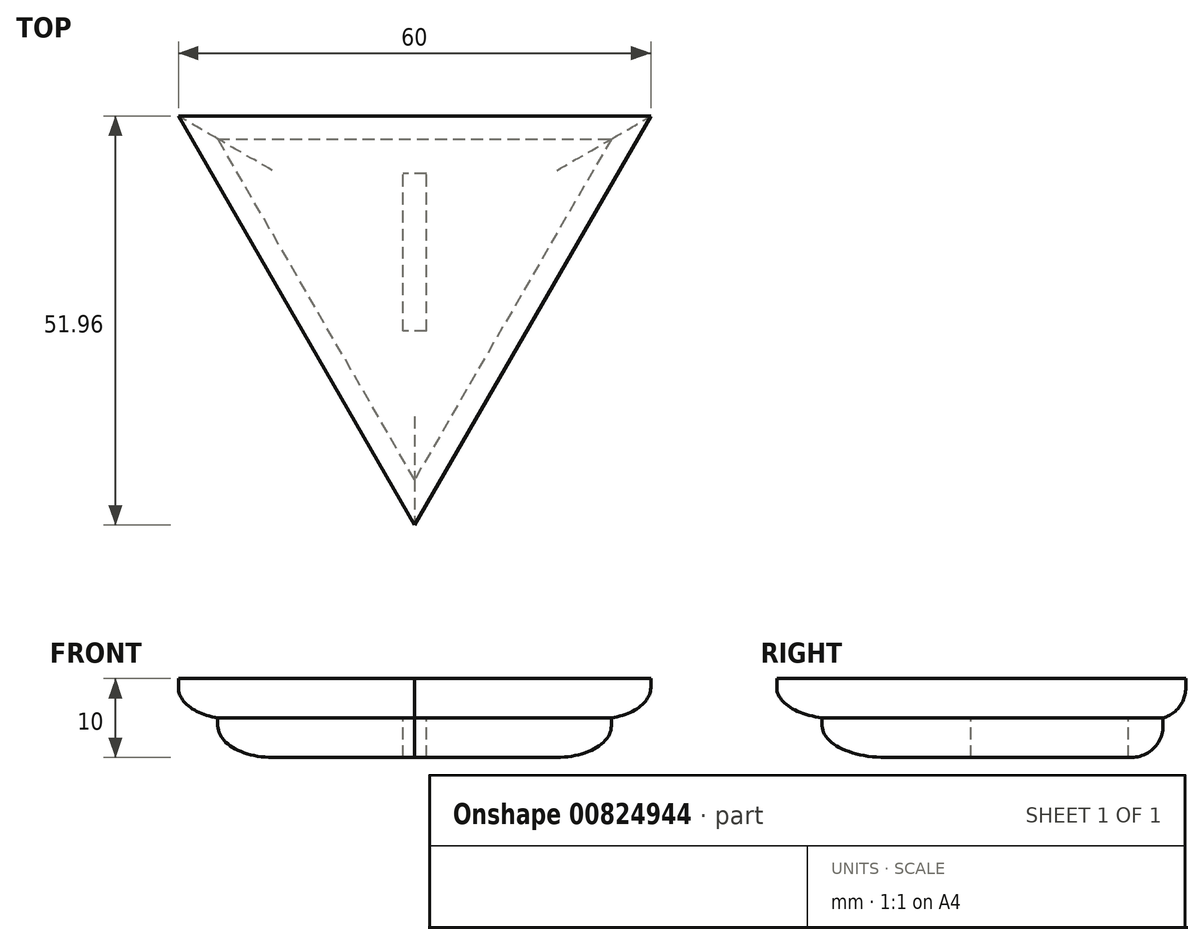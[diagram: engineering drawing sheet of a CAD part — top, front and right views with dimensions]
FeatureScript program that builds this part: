
annotation { "Feature Type Name" : "Feature", "Feature Type Description" : "" }
export const myFeature = defineFeature(function(context is Context, id is Id, definition is map)
    precondition{}
    {
        {
            var Q0;
            Q0=qCreatedBy(makeId("Top.planeOp"),FACE);
            var sketch = newSketch(context, id + "F0", { "sketchPlane" : qUnion([Q0])});
            skCircle(sketch, "E0.cCircle", {"center": v(0, 0) * mm, "radius": 14.43 * mm, "construction": true});
            skLineSegment(sketch, "E0.0", {"start": v(-25, 14.43) * mm, "end": v(25, 14.43) * mm});
            skLineSegment(sketch, "E0.1", {"start": v(25, 14.43) * mm, "end": v(0, -28.87) * mm});
            skLineSegment(sketch, "E0.2", {"start": v(0, -28.87) * mm, "end": v(-25, 14.43) * mm});
            skPoint(sketch, "E0.0.midPoint", {"position": v(0, 14.43) * mm});
            skCircle(sketch, "E1.cCircle", {"center": v(0, 0) * mm, "radius": 17.32 * mm, "construction": true});
            skLineSegment(sketch, "E1.0", {"start": v(-30, 17.32) * mm, "end": v(30, 17.32) * mm});
            skLineSegment(sketch, "E1.1", {"start": v(30, 17.32) * mm, "end": v(0, -34.64) * mm});
            skLineSegment(sketch, "E1.2", {"start": v(0, -34.64) * mm, "end": v(-30, 17.32) * mm});
            skPoint(sketch, "E1.0.midPoint", {"position": v(0, 17.32) * mm});
            skLineSegment(sketch, "E2.bottom", {"start": v(1.5, -10) * mm, "end": v(-1.5, -10) * mm});
            skLineSegment(sketch, "E2.top", {"start": v(1.5, 10) * mm, "end": v(-1.5, 10) * mm});
            skLineSegment(sketch, "E2.left", {"start": v(1.5, -10) * mm, "end": v(1.5, 10) * mm});
            skLineSegment(sketch, "E2.right", {"start": v(-1.5, -10) * mm, "end": v(-1.5, 10) * mm});
            skSolve(sketch);
        }
        {
            var Q0;
            Q0=makeQuery(id+"F0.imprint","IMPRINT",FACE,{"disambiguationData":[TD([[makeQuery(id+"F0.imprint","IMPRINT",EDGE,{"derivedFrom":sQuery(id+"F0.wireOp",EDGE,"E0.0")}),-1.0]])]});
            extrude(context, id + "F1", {"entities" : qUnion([Q0]), "oppositeDirection" : true, "depth" : 10 * mm, "offsetDistance" : 25 * mm});
        }
        {
            var Q0;
            Q0=makeQuery(id+"F0.imprint","IMPRINT",FACE,{"disambiguationData":[TD([[makeQuery(id+"F0.imprint","IMPRINT",EDGE,{"derivedFrom":sQuery(id+"F0.wireOp",EDGE,"E0.0")}),1.0]])]});
            var Q1;
            Q1=makeQuery(id+"F0.imprint","IMPRINT",FACE,{"disambiguationData":[TD([[makeQuery(id+"F0.imprint","IMPRINT",EDGE,{"derivedFrom":sQuery(id+"F0.wireOp",EDGE,"E2.bottom")}),-1.0]])]});
            extrude(context, id + "F2", {"entities" : qUnion([Q0, Q1]), "operationType" : NewBodyOperationType.ADD, "oppositeDirection" : true, "depth" : 5 * mm, "offsetDistance" : 25 * mm});
        }
        {
            var Q0;
            Q0=makeQuery(id+"F1.opExtrude","CAP_EDGE",EDGE,{"disambiguationData":[OSD([sQuery(id+"F0.wireOp",EDGE,"E0.0")])],"isStart":false});
            var Q1;
            Q1=makeQuery(id+"F2.opExtrude","CAP_EDGE",EDGE,{"disambiguationData":[OSD([sQuery(id+"F0.wireOp",EDGE,"E1.0")])],"isStart":false});
            var Q2;
            Q2=makeQuery(id+"F1.opExtrude","CAP_EDGE",EDGE,{"disambiguationData":[OSD([sQuery(id+"F0.wireOp",EDGE,"E0.1")])],"isStart":false});
            var Q3;
            Q3=makeQuery(id+"F1.opExtrude","CAP_EDGE",EDGE,{"disambiguationData":[OSD([sQuery(id+"F0.wireOp",EDGE,"E0.2")])],"isStart":false});
            var Q4;
            Q4=makeQuery(id+"F2.opExtrude","CAP_EDGE",EDGE,{"disambiguationData":[OSD([sQuery(id+"F0.wireOp",EDGE,"E1.1")])],"isStart":false});
            var Q5;
            Q5=makeQuery(id+"F2.opExtrude","CAP_EDGE",EDGE,{"disambiguationData":[OSD([sQuery(id+"F0.wireOp",EDGE,"E1.2")])],"isStart":false});
            fillet(context, id + "F3", {"entities" : qUnion([Q0, Q1, Q2, Q3, Q4, Q5]), "radius" : 4 * mm, "tangentPropagation" : true, "allowEdgeOverflow" : false});
        }
    });
